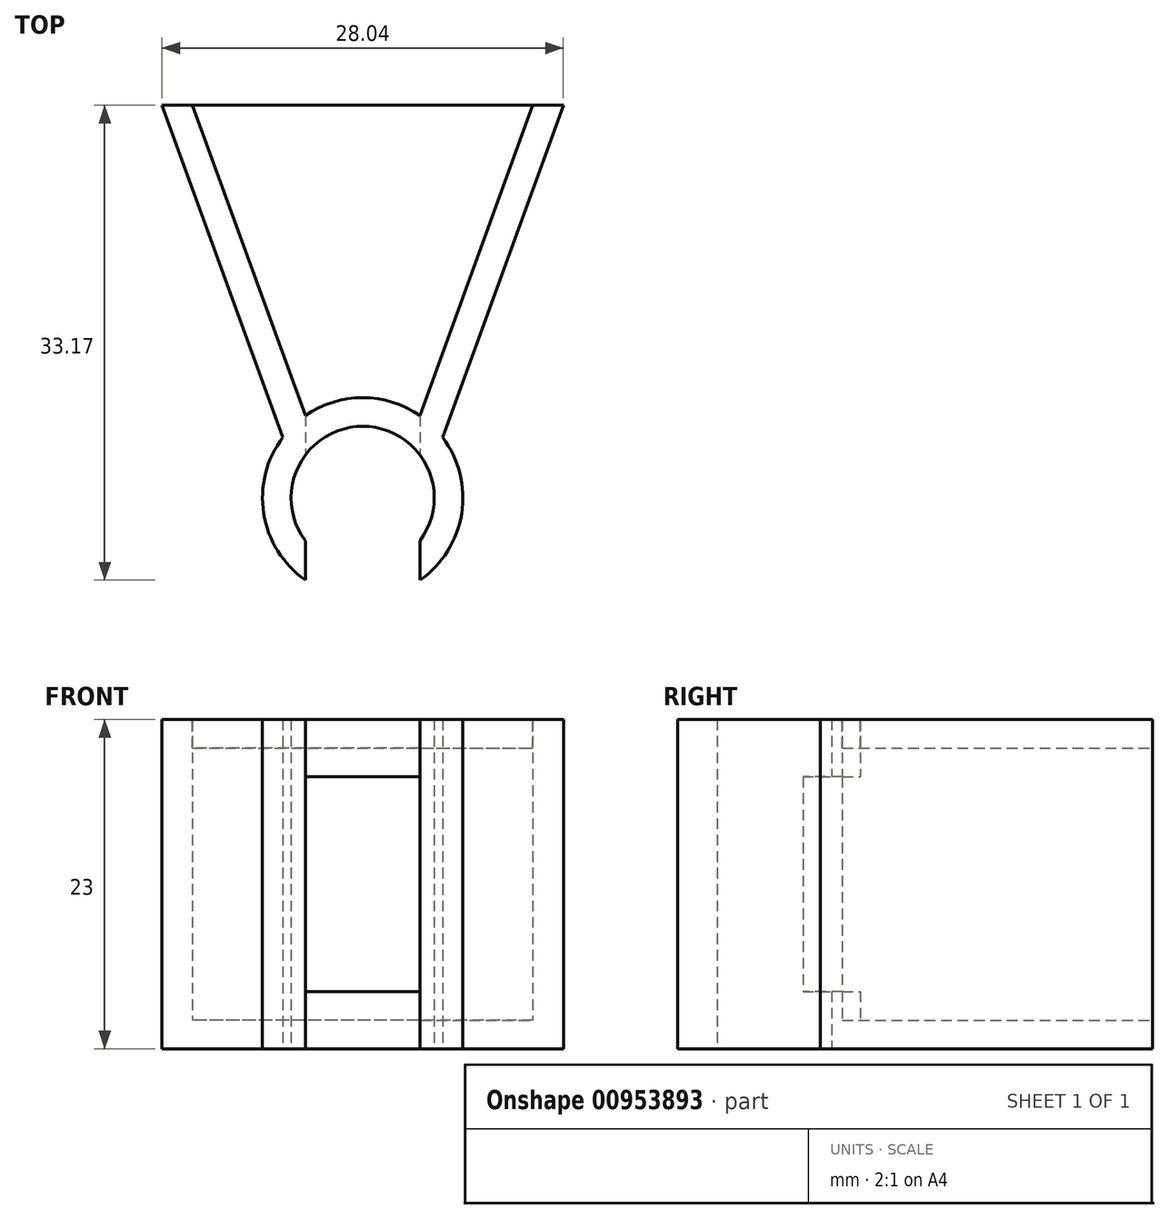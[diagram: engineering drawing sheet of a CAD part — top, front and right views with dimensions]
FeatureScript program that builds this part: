
annotation { "Feature Type Name" : "Feature", "Feature Type Description" : "" }
export const myFeature = defineFeature(function(context is Context, id is Id, definition is map)
    precondition{}
    {
        {
            var Q0;
            Q0=qCreatedBy(makeId("Top.planeOp"),FACE);
            var sketch = newSketch(context, id + "F0", { "sketchPlane" : qUnion([Q0])});
            skArc(sketch, "E0", {"start": v(4, -3) * mm, "mid": v(0, 5) * mm, "end": v(-4, -3) * mm});
            skArc(sketch, "E1", {"start": v(4, -5.74) * mm, "mid": v(0, 7) * mm, "end": v(-4, -5.74) * mm});
            skLineSegment(sketch, "E2", {"start": v(4, 19.63) * mm, "end": v(4, -19.13) * mm, "construction": true});
            skLineSegment(sketch, "E3.MirrorCS", {"start": v(-4, 19.63) * mm, "end": v(-4, -19.13) * mm, "construction": true});
            skLineSegment(sketch, "E4", {"start": v(-4, -3) * mm, "end": v(-4, -5.74) * mm});
            skLineSegment(sketch, "E5", {"start": v(4, -3) * mm, "end": v(4, -5.74) * mm});
            skLineSegment(sketch, "E6", {"start": v(4, 5.74) * mm, "end": v(11.9, 27.43) * mm});
            skLineSegment(sketch, "E7.MirrorCS", {"start": v(-4, 5.74) * mm, "end": v(-11.9, 27.43) * mm});
            skLineSegment(sketch, "E8.0", {"start": v(-5.58, 4.23) * mm, "end": v(-14.02, 27.43) * mm});
            skLineSegment(sketch, "E9.MirrorCS", {"start": v(5.58, 4.23) * mm, "end": v(14.02, 27.43) * mm});
            skLineSegment(sketch, "E10", {"start": v(-14.02, 27.43) * mm, "end": v(-11.9, 27.43) * mm});
            skLineSegment(sketch, "E11", {"start": v(14.02, 27.43) * mm, "end": v(11.9, 27.43) * mm});
            skPoint(sketch, "E12.orphan", {"position": v(-12.55, 29.24) * mm});
            skPoint(sketch, "E13.orphan", {"position": v(12.55, 29.24) * mm});
            skPoint(sketch, "E14.orphan", {"position": v(5.47, 3.94) * mm});
            skPoint(sketch, "E15.orphan", {"position": v(-5.47, 3.94) * mm});
            skSolve(sketch);
        }
        {
            var Q0;
            {var subQ0=sQuery(id+"F0.wireOp",EDGE,"E7.MirrorCS");Q0=makeQuery(id+"F0.imprint","IMPRINT",FACE,{"disambiguationData":[TD([[makeQuery(id+"F0.imprint","IMPRINT",EDGE,{"derivedFrom":subQ0}),1.0]])]});}
            var Q1;
            Q1=makeQuery(id+"F0.imprint","IMPRINT",FACE,{"disambiguationData":[TD([[makeQuery(id+"F0.imprint","IMPRINT",EDGE,{"derivedFrom":sQuery(id+"F0.wireOp",EDGE,"E0")}),-1.0]])]});
            var Q2;
            {var subQ0=sQuery(id+"F0.wireOp",EDGE,"E6");Q2=makeQuery(id+"F0.imprint","IMPRINT",FACE,{"disambiguationData":[TD([[makeQuery(id+"F0.imprint","IMPRINT",EDGE,{"derivedFrom":subQ0}),-1.0]])]});}
            extrude(context, id + "F1", {"entities" : qUnion([Q0, Q1, Q2]), "depth" : 23 * mm, "offsetDistance" : 25 * mm});
        }
        {
            var Q0;
            Q0=makeQuery(id+"F1.opExtrude","CAP_FACE",FACE,{"disambiguationData":[OSD([sQuery(id+"F0.wireOp",EDGE,"E0"),sQuery(id+"F0.wireOp",EDGE,"E1"),sQuery(id+"F0.wireOp",EDGE,"E4"),sQuery(id+"F0.wireOp",EDGE,"E5"),sQuery(id+"F0.wireOp",EDGE,"E6"),sQuery(id+"F0.wireOp",EDGE,"E7.MirrorCS"),sQuery(id+"F0.wireOp",EDGE,"E8.0"),sQuery(id+"F0.wireOp",EDGE,"E9.MirrorCS"),sQuery(id+"F0.wireOp",EDGE,"E10"),sQuery(id+"F0.wireOp",EDGE,"E11")])],"isStart":false});
            var sketch = newSketch(context, id + "F2", { "sketchPlane" : qUnion([Q0])});
            skLineSegment(sketch, "E16", {"start": v(-11.9, 27.43) * mm, "end": v(11.9, 27.43) * mm});
            skSolve(sketch);
        }
        {
            var Q0;
            Q0 = qSketchRegion(id + "F2", true);
            var Q1;
            Q1=makeQuery(id+"F2.imprint","IMPRINT",FACE,{"disambiguationData":[TD([[makeQuery(id+"F2.imprint","IMPRINT",EDGE,{"derivedFrom":sQuery(id+"F2.wireOp",EDGE,"E16")}),-1.0]])]});
            extrude(context, id + "F3", {"entities" : qUnion([Q0, Q1]), "oppositeDirection" : true, "depth" : 2 * mm, "offsetDistance" : 25 * mm});
        }
        {
            var Q0;
            Q0=makeQuery(id+"F1.opExtrude","CAP_FACE",FACE,{"disambiguationData":[OSD([sQuery(id+"F0.wireOp",EDGE,"E0"),sQuery(id+"F0.wireOp",EDGE,"E1"),sQuery(id+"F0.wireOp",EDGE,"E4"),sQuery(id+"F0.wireOp",EDGE,"E5"),sQuery(id+"F0.wireOp",EDGE,"E6"),sQuery(id+"F0.wireOp",EDGE,"E7.MirrorCS"),sQuery(id+"F0.wireOp",EDGE,"E8.0"),sQuery(id+"F0.wireOp",EDGE,"E9.MirrorCS"),sQuery(id+"F0.wireOp",EDGE,"E10"),sQuery(id+"F0.wireOp",EDGE,"E11")])],"isStart":true});
            var sketch = newSketch(context, id + "F4", { "sketchPlane" : qUnion([Q0])});
            skLineSegment(sketch, "E17", {"start": v(11.9, -27.43) * mm, "end": v(-11.9, -27.43) * mm});
            skSolve(sketch);
        }
        {
            var Q0;
            Q0 = qSketchRegion(id + "F4", true);
            var Q1;
            Q1=makeQuery(id+"F4.imprint","IMPRINT",FACE,{"disambiguationData":[TD([[makeQuery(id+"F4.imprint","IMPRINT",EDGE,{"derivedFrom":sQuery(id+"F4.wireOp",EDGE,"E17")}),-1.0]])]});
            extrude(context, id + "F5", {"entities" : qUnion([Q0, Q1]), "operationType" : NewBodyOperationType.ADD, "oppositeDirection" : true, "depth" : 2 * mm, "offsetDistance" : 25 * mm});
        }
        {
            var Q0;
            Q0=qCreatedBy(makeId("Front.planeOp"),FACE);
            var sketch = newSketch(context, id + "F6", { "sketchPlane" : qUnion([Q0])});
            skLineSegment(sketch, "E18.bottom", {"start": v(4, 19) * mm, "end": v(-4, 19) * mm});
            skLineSegment(sketch, "E18.top", {"start": v(4, 4) * mm, "end": v(-4, 4) * mm});
            skLineSegment(sketch, "E18.left", {"start": v(4, 19) * mm, "end": v(4, 4) * mm});
            skLineSegment(sketch, "E18.right", {"start": v(-4, 19) * mm, "end": v(-4, 4) * mm});
            skPoint(sketch, "E18.middle", {"position": v(0, 11.5) * mm});
            skSolve(sketch);
        }
        {
            var Q0;
            Q0 = qSketchRegion(id + "F6", true);
            extrude(context, id + "F7", {"entities" : qUnion([Q0]), "operationType" : NewBodyOperationType.REMOVE, "oppositeDirection" : true, "depth" : 25 * mm, "offsetDistance" : 25 * mm});
        }
    });
